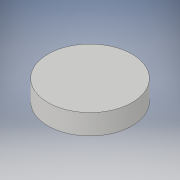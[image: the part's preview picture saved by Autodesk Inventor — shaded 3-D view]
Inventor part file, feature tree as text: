
AUTODESK INVENTOR PART (.ipt)
format: ipt  version: 2019 (Build 230136000, 136)  size: 212,480 bytes
history: native  units: mm
features: extrude x1, sketch x1
ambient origin geometry x8: Origin, YZ Plane, XZ Plane, XY Plane, X Axis, Y Axis, Z Axis, Center Point
bodies: Solid1 (feature_tree)
feature tree (2):
  extrude  "Extrusion1"  Depth=1.3mm TaperAngle=0.0deg
  sketch  "Sketch1"  dims[d0=5.4mm d1=1.3mm d2=0.0mm]
